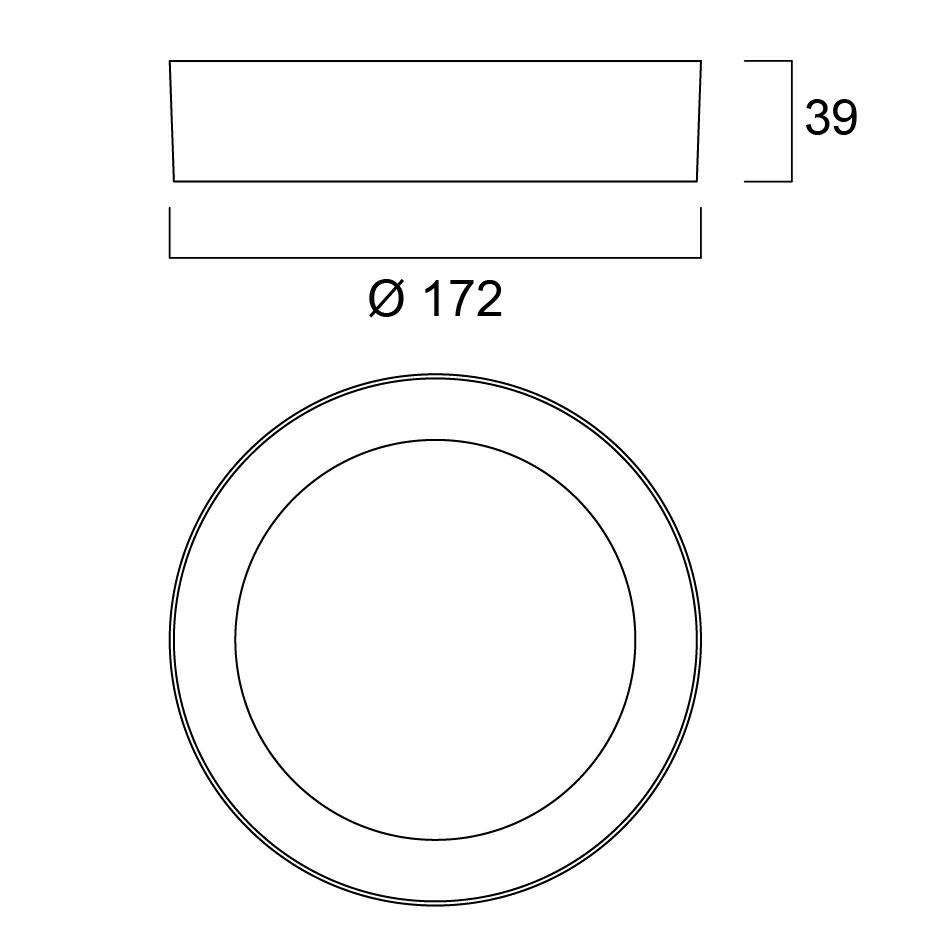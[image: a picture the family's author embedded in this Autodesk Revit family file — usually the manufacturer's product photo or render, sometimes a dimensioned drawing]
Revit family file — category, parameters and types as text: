
# Revit family: 0053903
name_source: partatom
category: Lighting Fixtures
revit_build: Autodesk Revit 2016 (Build: 20150220_1215(x64)
units: mm (PartAtom-declared; Revit-internal decimal feet)

## family parameters
Cut with Voids When Loaded = No
Host = Face
Light Source = Yes
OmniClass Number = 23.80.70.00
OmniClass Title = Lighting
Part Type = Normal
Room Calculation Point = No
Round Connector Dimension = Use Diameter
Shared = No

## types (1)
- 0053903 ST eco Downlight Flat 172 1150lm 840 DIM S
    Apparent Load = 13 VA
    Assembly Code = D5020200
    AssetType = Fixed
    ClassificationName = Uniclass2015
    ClassificationValue = EF_70_80
    Color Filter = 16777215
    Cost = 0 $
    Default Elevation = 1219 mm
    Description = Integrated LED surface mounted downlight providing 1190 fixture lumens at a wattage of 13W giving a high efficacy of 92lm/W. Fitting includes Leading/Trailing edge phase dimmable driver and has a round outer dimmension of of 172x172x39mm with an IP20 and IK02 rating providing uniform distribution with an Opal diffuser and 110° beam angle. Provided including a Loop in Loop out box and built with a white aluminium housing.
    Dimming Lamp Color Temperature Shift = <None>
    DimmingControlOptions = Dimmable
    DocumentationLiterature = http://www.sylvania-lighting.com
    DurationUnit = hours
    ElectricShockClassification = Class II
    Emit Shape Visible in Rendering = No
    Emit from Circle Diameter = 129 mm
    ExpectedLife = 50000
    IfcExportAs = IfcLightFixtureType
    IfcExportType = IfcLightFixtureType
    ImpactProtectionIndex = IK06
    IngressProtection = IP20
    InputNominalFrequency = 50/60 Hz
    InputVoltage = 220-240V~
    Keynote = 16500
    Lamp = LED
    LampColourRenderingIndex = 80
    LampColourTemperature = 4000 K
    LampNominalLuminous = 1150 lm
    LampsType = LED
    LuminousEfficacy = 88.46 lm/W
    Manufacturer = Feilo Sylvania
    ManufacturerName = Feilo Sylvania
    Material = aluminium housing, polystyrene diffuser
    Material_1_FEILO = Body-Sylvania-SylflatSurface-White
    Material_2_FEILO = LED-Sylvania-SylflatSurface
    Material_3_FEILO = <By Category>
    Material_4_FEILO = <By Category>
    Model = ST eco Downlight Flat 172 1150lm 840 DIM S
    ModelNumber = 0053903
    ModelReference = ST eco Downlight Flat 172 1150lm 840 DIM S
    Name = ST eco Downlight Flat 172 1150lm 840 DIM S
    NominalDepth = 172 mm  [stored 0.564304 ft]
    NominalHeight = 39 mm  [stored 0.127953 ft]
    NominalLength = 172 mm  [stored 0.564304 ft]
    Photometric Web File = 0053903.ies
    PowerConsumption = 13 W
    PowerFactor = 0.9
    RadiusDiffuser_FEILO = 7 mm  [stored 0.0229659 ft]
    RadiusSquare_FEILO = 10 mm  [stored 0.0328084 ft]
    Round_FEILO = Yes
    Square_FEILO = No
    Tilt Angle = -90.00°
    Type Image = <None>
    TypeName = ST eco Downlight Flat 172 1150lm 840 DIM S
    URL = http://www.sylvania-lighting.com
    Voltage = 230 V
    Weight = 10.24 kg
    WidthDiffuser_FEILO = 129 mm
    Width_FEILO = 172 mm  [stored 0.564304 ft]

note: [stored X ft] marks values corroborated as IEEE doubles in the binary element streams (Revit-internal decimal feet)

## geometry (parser evidence)
native form markers: Sweep x1
no freeform markers — native parametric forms only
